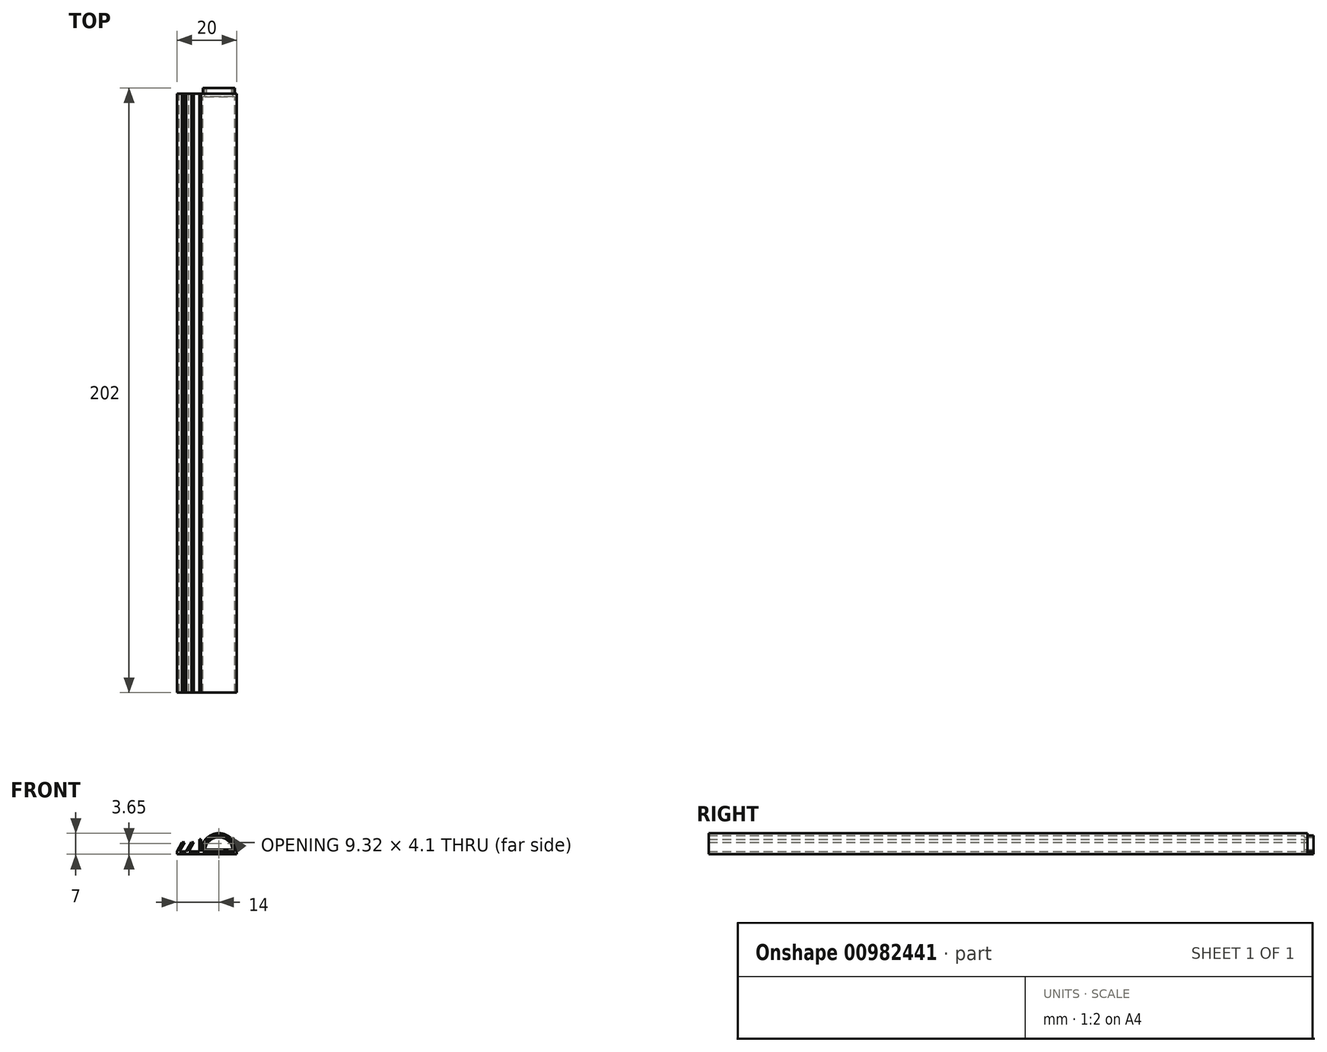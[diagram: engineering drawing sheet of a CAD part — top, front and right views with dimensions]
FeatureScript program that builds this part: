
annotation { "Feature Type Name" : "Feature", "Feature Type Description" : "" }
export const myFeature = defineFeature(function(context is Context, id is Id, definition is map)
    precondition{}
    {
        {
            var Q0;
            Q0=qCreatedBy(makeId("Front.planeOp"),FACE);
            var sketch = newSketch(context, id + "F0", { "sketchPlane" : qUnion([Q0])});
            skLineSegment(sketch, "E0", {"start": v(0, 0) * mm, "end": v(12, 0) * mm});
            skLineSegment(sketch, "E1", {"start": v(0, 1) * mm, "end": v(0, 5) * mm});
            skLineSegment(sketch, "E2", {"start": v(0, 5) * mm, "end": v(-0.5, 5) * mm});
            skLineSegment(sketch, "E3", {"start": v(-0.5, 5) * mm, "end": v(-0.5, 1) * mm});
            skLineSegment(sketch, "E4", {"start": v(-0.5, 1) * mm, "end": v(-4.07, 1) * mm});
            skLineSegment(sketch, "E5", {"start": v(-4.07, 1) * mm, "end": v(-2.34, 4) * mm});
            skLineSegment(sketch, "E6", {"start": v(-2.34, 4) * mm, "end": v(-3.15, 4) * mm});
            skLineSegment(sketch, "E7", {"start": v(-3.15, 4) * mm, "end": v(-4.88, 1) * mm});
            skLineSegment(sketch, "E8", {"start": v(-4.88, 1) * mm, "end": v(-7.2, 1) * mm});
            skLineSegment(sketch, "E9", {"start": v(-7.2, 1) * mm, "end": v(-5.46, 4) * mm});
            skLineSegment(sketch, "E10", {"start": v(-5.46, 4) * mm, "end": v(-6.27, 4) * mm});
            skLineSegment(sketch, "E11", {"start": v(-6.27, 4) * mm, "end": v(-8, 1) * mm});
            skLineSegment(sketch, "E12", {"start": v(-8, 1) * mm, "end": v(-8, 0) * mm});
            skLineSegment(sketch, "E13", {"start": v(-8, 0) * mm, "end": v(0, 0) * mm});
            skLineSegment(sketch, "E14", {"start": v(12, 0) * mm, "end": v(12, 1) * mm});
            skArc(sketch, "E15", {"start": v(12, 1) * mm, "mid": v(6, 7) * mm, "end": v(0, 1) * mm});
            skArc(sketch, "E16.0", {"start": v(11.3, 1) * mm, "mid": v(6, 6.3) * mm, "end": v(0.7, 1) * mm});
            skLineSegment(sketch, "E17", {"start": v(0.7, 1) * mm, "end": v(11.3, 1) * mm});
            skSolve(sketch);
        }
        {
            var Q0;
            Q0 = qSketchRegion(id + "F0", true);
            extrude(context, id + "F1", {"entities" : qUnion([Q0]), "depth" : 200 * mm, "offsetDistance" : 25 * mm});
        }
        {
            var Q0;
            Q0=qCreatedBy(makeId("Front.planeOp"),FACE);
            var sketch = newSketch(context, id + "F2", { "sketchPlane" : qUnion([Q0])});
            skArc(sketch, "E18.0", {"start": v(11.1, 1.2) * mm, "mid": v(6, 6.1) * mm, "end": v(0.9, 1.2) * mm});
            skLineSegment(sketch, "E18.1", {"start": v(0.9, 1.2) * mm, "end": v(11.1, 1.2) * mm});
            skArc(sketch, "E19.0", {"start": v(10.66, 1.6) * mm, "mid": v(6, 5.7) * mm, "end": v(1.34, 1.6) * mm});
            skLineSegment(sketch, "E19.1", {"start": v(1.34, 1.6) * mm, "end": v(10.66, 1.6) * mm});
            skArc(sketch, "E20.0", {"start": v(11.3, 1) * mm, "mid": v(6, 6.3) * mm, "end": v(0.7, 1) * mm});
            skLineSegment(sketch, "E21", {"start": v(11.3, 1) * mm, "end": v(0.7, 1) * mm});
            skLineSegment(sketch, "E22.bottom", {"start": v(11.1, 1.2) * mm, "end": v(10.2, 1.2) * mm});
            skLineSegment(sketch, "E22.top", {"start": v(11.2, 0) * mm, "end": v(10.2, 0) * mm});
            skLineSegment(sketch, "E22.right", {"start": v(10.2, 1.2) * mm, "end": v(10.2, 0) * mm});
            skLineSegment(sketch, "E23.bottom", {"start": v(0.9, 1.2) * mm, "end": v(1.8, 1.2) * mm});
            skLineSegment(sketch, "E23.top", {"start": v(0.8, 0) * mm, "end": v(1.8, 0) * mm});
            skLineSegment(sketch, "E23.right", {"start": v(1.8, 1.2) * mm, "end": v(1.8, 0) * mm});
            skLineSegment(sketch, "E24", {"start": v(11.11, 1.2) * mm, "end": v(11.11, 0) * mm});
            skLineSegment(sketch, "E25", {"start": v(0.86, 1.2) * mm, "end": v(0.86, 0) * mm});
            skSolve(sketch);
        }
        {
            var Q0;
            Q0=makeQuery(id+"F2.imprint","IMPRINT",FACE,{"disambiguationData":[TD([[makeQuery(id+"F2.imprint","IMPRINT",EDGE,{"derivedFrom":sQuery(id+"F2.wireOp",EDGE,"E18.0")}),-1.0]])]});
            var Q1;
            Q1=makeQuery(id+"F2.imprint","IMPRINT",FACE,{"disambiguationData":[TD([[makeQuery(id+"F2.imprint","IMPRINT",EDGE,{"derivedFrom":sQuery(id+"F2.wireOp",EDGE,"E18.0")}),1.0]])]});
            var Q2;
            {var subQ0=sQuery(id+"F2.wireOp",EDGE,"E22.right");var subQ1=sQuery(id+"F2.wireOp",EDGE,"E18.1");var subQ2=makeQuery(id+"F2.imprint","INTERSECT",VERTEX,{"derivedFrom":[subQ1,subQ0]});Q2=makeQuery(id+"F2.imprint","IMPRINT",FACE,{"disambiguationData":[TD([[makeQuery(id+"F2.imprint","IMPRINT",EDGE,{"disambiguationData":[TD([[subQ2,-1.0]])],"derivedFrom":subQ1}),-1.0]])]});}
            var Q3;
            {var subQ0=sQuery(id+"F2.wireOp",EDGE,"E23.right");var subQ1=sQuery(id+"F2.wireOp",EDGE,"E18.1");var subQ2=makeQuery(id+"F2.imprint","INTERSECT",VERTEX,{"derivedFrom":[subQ1,subQ0]});Q3=makeQuery(id+"F2.imprint","IMPRINT",FACE,{"disambiguationData":[TD([[makeQuery(id+"F2.imprint","IMPRINT",EDGE,{"disambiguationData":[TD([[subQ2,-1.0]])],"derivedFrom":subQ1}),-1.0]])]});}
            var Q4;
            {var subQ0=sQuery(id+"F2.wireOp",EDGE,"E23.right");var subQ1=sQuery(id+"F2.wireOp",EDGE,"E18.1");var subQ2=makeQuery(id+"F2.imprint","INTERSECT",VERTEX,{"derivedFrom":[subQ1,subQ0]});Q4=makeQuery(id+"F2.imprint","IMPRINT",FACE,{"disambiguationData":[TD([[makeQuery(id+"F2.imprint","IMPRINT",EDGE,{"disambiguationData":[TD([[subQ2,1.0]])],"derivedFrom":subQ1}),-1.0]])]});}
            extrude(context, id + "F3", {"entities" : qUnion([Q0, Q1, Q2, Q3, Q4]), "operationType" : NewBodyOperationType.ADD, "depth" : 1 * mm, "offsetDistance" : 25 * mm});
        }
        {
            var Q0;
            Q0=makeQuery(id+"F2.imprint","IMPRINT",FACE,{"disambiguationData":[TD([[makeQuery(id+"F2.imprint","IMPRINT",EDGE,{"derivedFrom":sQuery(id+"F2.wireOp",EDGE,"E18.0")}),1.0]])]});
            var Q1;
            {var subQ0=sQuery(id+"F2.wireOp",EDGE,"E22.right");var subQ1=sQuery(id+"F2.wireOp",EDGE,"E21");var subQ2=makeQuery(id+"F2.imprint","INTERSECT",VERTEX,{"derivedFrom":[subQ1,subQ0]});Q1=makeQuery(id+"F2.imprint","IMPRINT",FACE,{"disambiguationData":[TD([[makeQuery(id+"F2.imprint","IMPRINT",EDGE,{"disambiguationData":[TD([[subQ2,1.0]])],"derivedFrom":subQ1}),1.0]])]});}
            var Q2;
            {var subQ0=sQuery(id+"F2.wireOp",EDGE,"E23.right");var subQ1=sQuery(id+"F2.wireOp",EDGE,"E21");var subQ2=makeQuery(id+"F2.imprint","INTERSECT",VERTEX,{"derivedFrom":[subQ1,subQ0]});Q2=makeQuery(id+"F2.imprint","IMPRINT",FACE,{"disambiguationData":[TD([[makeQuery(id+"F2.imprint","IMPRINT",EDGE,{"disambiguationData":[TD([[subQ2,-1.0]])],"derivedFrom":subQ1}),1.0]])]});}
            var Q3;
            {var subQ0=sQuery(id+"F2.wireOp",EDGE,"E22.right");var subQ1=sQuery(id+"F2.wireOp",EDGE,"E18.1");var subQ2=makeQuery(id+"F2.imprint","INTERSECT",VERTEX,{"derivedFrom":[subQ1,subQ0]});Q3=makeQuery(id+"F2.imprint","IMPRINT",FACE,{"disambiguationData":[TD([[makeQuery(id+"F2.imprint","IMPRINT",EDGE,{"disambiguationData":[TD([[subQ2,-1.0]])],"derivedFrom":subQ1}),-1.0]])]});}
            var Q4;
            {var subQ0=sQuery(id+"F2.wireOp",EDGE,"E23.right");var subQ1=sQuery(id+"F2.wireOp",EDGE,"E18.1");var subQ2=makeQuery(id+"F2.imprint","INTERSECT",VERTEX,{"derivedFrom":[subQ1,subQ0]});Q4=makeQuery(id+"F2.imprint","IMPRINT",FACE,{"disambiguationData":[TD([[makeQuery(id+"F2.imprint","IMPRINT",EDGE,{"disambiguationData":[TD([[subQ2,1.0]])],"derivedFrom":subQ1}),-1.0]])]});}
            extrude(context, id + "F4", {"entities" : qUnion([Q0, Q1, Q2, Q3, Q4]), "operationType" : NewBodyOperationType.ADD, "oppositeDirection" : true, "depth" : 2 * mm, "offsetDistance" : 25 * mm});
        }
    });
